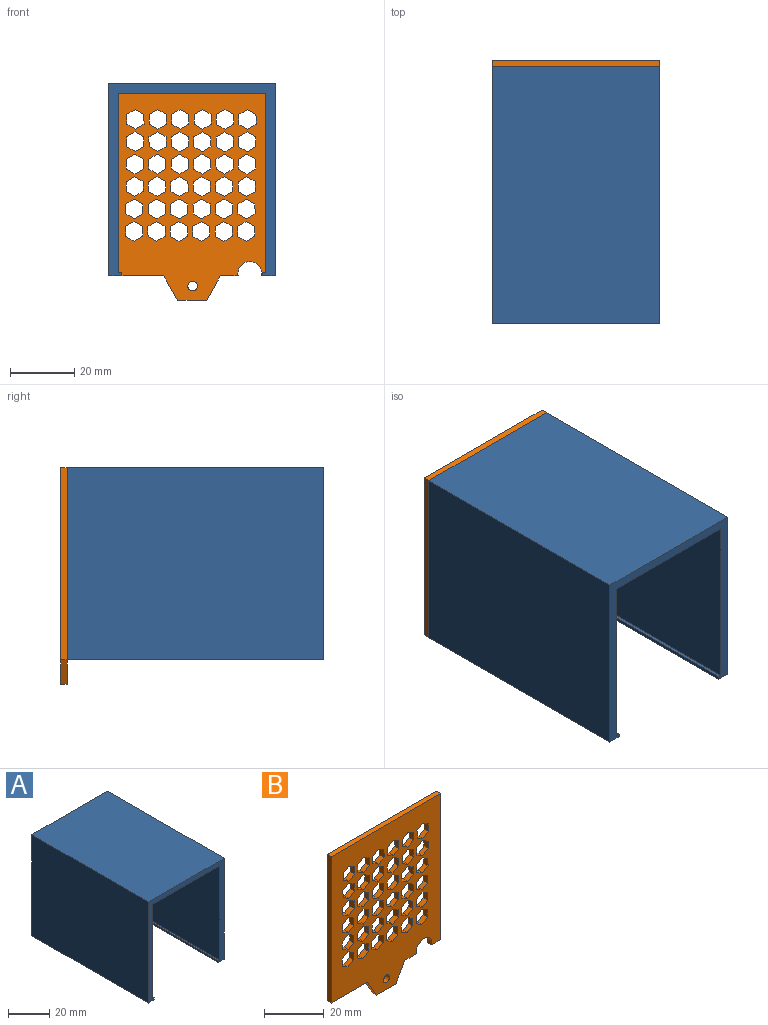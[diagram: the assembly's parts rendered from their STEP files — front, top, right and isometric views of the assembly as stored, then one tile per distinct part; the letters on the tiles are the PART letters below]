
ASSEMBLY  parts=2 mates=1
PART A: 14 faces, bbox 52x80x60 mm
  f0: plane 80x1mm, normal (1,0,0), area 80mm2, adj f1,f11,f12,f13
  f1: plane 80x1mm, normal (0,0,1), area 80mm2, adj f0,f2,f12,f13
  f2: plane 80x56mm, normal (1,0,0), area 4480mm2, adj f1,f3,f12,f13
  f3: plane 80x46mm, normal (0,0,-1), area 3680mm2, adj f2,f4,f12,f13
  f4: plane 80x56mm, normal (-1,0,0), area 4480mm2, adj f3,f5,f12,f13
  f5: plane 80x1mm, normal (0,0,1), area 80mm2, adj f4,f6,f12,f13
  f6: plane 80x1mm, normal (-1,0,0), area 80mm2, adj f5,f7,f12,f13
  f7: plane 80x4mm, normal (0,0,-1), area 320mm2, adj f6,f8,f12,f13
  f8: plane 80x60mm, normal (1,0,0), area 4800mm2, adj f7,f9,f12,f13
  f9: plane 80x52mm, normal (0,0,1), area 4160mm2, adj f8,f10,f12,f13
  f10: plane 80x60mm, normal (-1,0,0), area 4800mm2, adj f9,f11,f12,f13
  f11: plane 80x4mm, normal (0,0,-1), area 320mm2, adj f0,f10,f12,f13
  f12: plane 60x52mm, normal (0,-1,0), area 500mm2, adj f0,f1,f2,f3,f4,f5,f6,f7
  f13: plane 60x52mm, normal (0,1,0), area 500mm2, adj f0,f1,f2,f3,f4,f5,f6,f7
PART B: 229 faces, bbox 52x2x67.5 mm
  f0: plane 5.6x2mm, normal (0,0,-1), area 11.2mm2, adj f3,f4,f224,f228
  f1: plane 4.35x2mm, normal (0,0,-1), area 8.7mm2, adj f3,f4,f5,f228
  f2: plane 17.18x2mm, normal (0,0,-1), area 34.4mm2, adj f3,f4,f7,f225
  f3: plane 67.54x52mm, normal (0,1,0), area 2293.7mm2, adj f0,f1,f2,f5,f6,f7,f8,f9
  f4: plane 67.54x52mm, normal (0,-1,0), area 2293.7mm2, adj f0,f1,f2,f5,f6,f7,f8,f9
  f5: plane 60x2mm, normal (1,0,0), area 120mm2, adj f1,f3,f4,f6
  f6: plane 52x2mm, normal (0,0,1), area 104mm2, adj f3,f4,f5,f7
  f7: plane 60x2mm, normal (-1,0,0), area 120mm2, adj f2,f3,f4,f6
  f8: plane 3.09x2mm, normal (1,0,0.01), area 6.2mm2, adj f3,f4,f9,f13
  f9: plane 2.66x2mm, normal (0.51,0,-0.86), area 6.2mm2, adj f3,f4,f8,f10
  f10: plane 2.69x2mm, normal (-0.49,0,-0.87), area 6.2mm2, adj f3,f4,f9,f11
  f11: plane 3.09x2mm, normal (-1,0,-0.01), area 6.2mm2, adj f3,f4,f10,f12
  f12: plane 2.66x2mm, normal (-0.51,0,0.86), area 6.2mm2, adj f3,f4,f11,f13
  f13: plane 2.69x2mm, normal (0.49,0,0.87), area 6.2mm2, adj f3,f4,f8,f12
  f14: plane 2.66x2mm, normal (0.51,0,-0.86), area 6.2mm2, adj f3,f4,f15,f19
  f15: plane 2.69x2mm, normal (-0.49,0,-0.87), area 6.2mm2, adj f3,f4,f14,f16
  f16: plane 3.09x2mm, normal (-1,0,-0.01), area 6.2mm2, adj f3,f4,f15,f17
  f17: plane 2.66x2mm, normal (-0.51,0,0.86), area 6.2mm2, adj f3,f4,f16,f18
  f18: plane 2.69x2mm, normal (0.49,0,0.87), area 6.2mm2, adj f3,f4,f17,f19
  f19: plane 3.09x2mm, normal (1,0,0.01), area 6.2mm2, adj f3,f4,f14,f18
  f20: plane 3.09x2mm, normal (1,0,0.01), area 6.2mm2, adj f3,f4,f21,f25
  f21: plane 2.66x2mm, normal (0.51,0,-0.86), area 6.2mm2, adj f3,f4,f20,f22
  f22: plane 2.69x2mm, normal (-0.49,0,-0.87), area 6.2mm2, adj f3,f4,f21,f23
  f23: plane 3.09x2mm, normal (-1,0,-0.01), area 6.2mm2, adj f3,f4,f22,f24
  f24: plane 2.66x2mm, normal (-0.51,0,0.86), area 6.2mm2, adj f3,f4,f23,f25
  f25: plane 2.69x2mm, normal (0.49,0,0.87), area 6.2mm2, adj f3,f4,f20,f24
  f26: plane 2.69x2mm, normal (-0.49,0,-0.87), area 6.2mm2, adj f3,f4,f27,f31
  f27: plane 3.09x2mm, normal (-1,0,-0.01), area 6.2mm2, adj f3,f4,f26,f28
  f28: plane 2.66x2mm, normal (-0.51,0,0.86), area 6.2mm2, adj f3,f4,f27,f29
  f29: plane 2.69x2mm, normal (0.49,0,0.87), area 6.2mm2, adj f3,f4,f28,f30
  f30: plane 3.09x2mm, normal (1,0,0.01), area 6.2mm2, adj f3,f4,f29,f31
  f31: plane 2.66x2mm, normal (0.51,0,-0.86), area 6.2mm2, adj f3,f4,f26,f30
  f32: plane 3.09x2mm, normal (-1,0,-0.01), area 6.2mm2, adj f3,f4,f33,f37
  f33: plane 2.66x2mm, normal (-0.51,0,0.86), area 6.2mm2, adj f3,f4,f32,f34
  f34: plane 2.69x2mm, normal (0.49,0,0.87), area 6.2mm2, adj f3,f4,f33,f35
  f35: plane 3.09x2mm, normal (1,0,0.01), area 6.2mm2, adj f3,f4,f34,f36
  f36: plane 2.66x2mm, normal (0.51,0,-0.86), area 6.2mm2, adj f3,f4,f35,f37
  f37: plane 2.69x2mm, normal (-0.49,0,-0.87), area 6.2mm2, adj f3,f4,f32,f36
  f38: plane 2.66x2mm, normal (0.51,0,-0.86), area 6.2mm2, adj f3,f4,f39,f43
  f39: plane 2.69x2mm, normal (-0.49,0,-0.87), area 6.2mm2, adj f3,f4,f38,f40
  f40: plane 3.09x2mm, normal (-1,0,-0.01), area 6.2mm2, adj f3,f4,f39,f41
  f41: plane 2.66x2mm, normal (-0.51,0,0.86), area 6.2mm2, adj f3,f4,f40,f42
  f42: plane 2.69x2mm, normal (0.49,0,0.87), area 6.2mm2, adj f3,f4,f41,f43
  f43: plane 3.09x2mm, normal (1,0,0.01), area 6.2mm2, adj f3,f4,f38,f42
  f44: plane 3.09x2mm, normal (1,0,0.01), area 6.2mm2, adj f3,f4,f45,f49
  f45: plane 2.66x2mm, normal (0.51,0,-0.86), area 6.2mm2, adj f3,f4,f44,f46
  f46: plane 2.69x2mm, normal (-0.49,0,-0.87), area 6.2mm2, adj f3,f4,f45,f47
  f47: plane 3.09x2mm, normal (-1,0,-0.01), area 6.2mm2, adj f3,f4,f46,f48
  f48: plane 2.66x2mm, normal (-0.51,0,0.86), area 6.2mm2, adj f3,f4,f47,f49
  f49: plane 2.69x2mm, normal (0.49,0,0.87), area 6.2mm2, adj f3,f4,f44,f48
  f50: plane 2.69x2mm, normal (-0.49,0,-0.87), area 6.2mm2, adj f3,f4,f51,f55
  f51: plane 3.09x2mm, normal (-1,0,-0.01), area 6.2mm2, adj f3,f4,f50,f52
  f52: plane 2.66x2mm, normal (-0.51,0,0.86), area 6.2mm2, adj f3,f4,f51,f53
  f53: plane 2.69x2mm, normal (0.49,0,0.87), area 6.2mm2, adj f3,f4,f52,f54
  f54: plane 3.09x2mm, normal (1,0,0.01), area 6.2mm2, adj f3,f4,f53,f55
  f55: plane 2.66x2mm, normal (0.51,0,-0.86), area 6.2mm2, adj f3,f4,f50,f54
  f56: plane 2.69x2mm, normal (-0.49,0,-0.87), area 6.2mm2, adj f3,f4,f57,f61
  f57: plane 3.09x2mm, normal (-1,0,-0.01), area 6.2mm2, adj f3,f4,f56,f58
  f58: plane 2.66x2mm, normal (-0.51,0,0.86), area 6.2mm2, adj f3,f4,f57,f59
  f59: plane 2.69x2mm, normal (0.49,0,0.87), area 6.2mm2, adj f3,f4,f58,f60
  f60: plane 3.09x2mm, normal (1,0,0.01), area 6.2mm2, adj f3,f4,f59,f61
  f61: plane 2.66x2mm, normal (0.51,0,-0.86), area 6.2mm2, adj f3,f4,f56,f60
  f62: plane 2.69x2mm, normal (-0.49,0,-0.87), area 6.2mm2, adj f3,f4,f63,f67
  f63: plane 3.09x2mm, normal (-1,0,-0.01), area 6.2mm2, adj f3,f4,f62,f64
  f64: plane 2.66x2mm, normal (-0.51,0,0.86), area 6.2mm2, adj f3,f4,f63,f65
  f65: plane 2.69x2mm, normal (0.49,0,0.87), area 6.2mm2, adj f3,f4,f64,f66
  f66: plane 3.09x2mm, normal (1,0,0.01), area 6.2mm2, adj f3,f4,f65,f67
  f67: plane 2.66x2mm, normal (0.51,0,-0.86), area 6.2mm2, adj f3,f4,f62,f66
  f68: plane 2.69x2mm, normal (-0.49,0,-0.87), area 6.2mm2, adj f3,f4,f69,f73
  f69: plane 3.09x2mm, normal (-1,0,-0.01), area 6.2mm2, adj f3,f4,f68,f70
  f70: plane 2.66x2mm, normal (-0.51,0,0.86), area 6.2mm2, adj f3,f4,f69,f71
  f71: plane 2.69x2mm, normal (0.49,0,0.87), area 6.2mm2, adj f3,f4,f70,f72
  f72: plane 3.09x2mm, normal (1,0,0.01), area 6.2mm2, adj f3,f4,f71,f73
  f73: plane 2.66x2mm, normal (0.51,0,-0.86), area 6.2mm2, adj f3,f4,f68,f72
  f74: plane 3.09x2mm, normal (1,0,0.01), area 6.2mm2, adj f3,f4,f75,f79
  f75: plane 2.66x2mm, normal (0.51,0,-0.86), area 6.2mm2, adj f3,f4,f74,f76
  f76: plane 2.69x2mm, normal (-0.49,0,-0.87), area 6.2mm2, adj f3,f4,f75,f77
  f77: plane 3.09x2mm, normal (-1,0,-0.01), area 6.2mm2, adj f3,f4,f76,f78
  f78: plane 2.66x2mm, normal (-0.51,0,0.86), area 6.2mm2, adj f3,f4,f77,f79
  f79: plane 2.69x2mm, normal (0.49,0,0.87), area 6.2mm2, adj f3,f4,f74,f78
  f80: plane 2.66x2mm, normal (0.51,0,-0.86), area 6.2mm2, adj f3,f4,f81,f85
  f81: plane 2.69x2mm, normal (-0.49,0,-0.87), area 6.2mm2, adj f3,f4,f80,f82
  f82: plane 3.09x2mm, normal (-1,0,-0.01), area 6.2mm2, adj f3,f4,f81,f83
  f83: plane 2.66x2mm, normal (-0.51,0,0.86), area 6.2mm2, adj f3,f4,f82,f84
  f84: plane 2.69x2mm, normal (0.49,0,0.87), area 6.2mm2, adj f3,f4,f83,f85
  f85: plane 3.09x2mm, normal (1,0,0.01), area 6.2mm2, adj f3,f4,f80,f84
  f86: plane 2.66x2mm, normal (0.51,0,-0.86), area 6.2mm2, adj f3,f4,f87,f91
  f87: plane 2.69x2mm, normal (-0.49,0,-0.87), area 6.2mm2, adj f3,f4,f86,f88
  f88: plane 3.09x2mm, normal (-1,0,-0.01), area 6.2mm2, adj f3,f4,f87,f89
  f89: plane 2.66x2mm, normal (-0.51,0,0.86), area 6.2mm2, adj f3,f4,f88,f90
  f90: plane 2.69x2mm, normal (0.49,0,0.87), area 6.2mm2, adj f3,f4,f89,f91
  f91: plane 3.09x2mm, normal (1,0,0.01), area 6.2mm2, adj f3,f4,f86,f90
  f92: plane 2.66x2mm, normal (0.51,0,-0.86), area 6.2mm2, adj f3,f4,f93,f97
  f93: plane 2.69x2mm, normal (-0.49,0,-0.87), area 6.2mm2, adj f3,f4,f92,f94
  f94: plane 3.09x2mm, normal (-1,0,-0.01), area 6.2mm2, adj f3,f4,f93,f95
  f95: plane 2.66x2mm, normal (-0.51,0,0.86), area 6.2mm2, adj f3,f4,f94,f96
  f96: plane 2.69x2mm, normal (0.49,0,0.87), area 6.2mm2, adj f3,f4,f95,f97
  f97: plane 3.09x2mm, normal (1,0,0.01), area 6.2mm2, adj f3,f4,f92,f96
  f98: plane 2.66x2mm, normal (0.51,0,-0.86), area 6.2mm2, adj f3,f4,f99,f103
  f99: plane 2.69x2mm, normal (-0.49,0,-0.87), area 6.2mm2, adj f3,f4,f98,f100
  f100: plane 3.09x2mm, normal (-1,0,-0.01), area 6.2mm2, adj f3,f4,f99,f101
  f101: plane 2.66x2mm, normal (-0.51,0,0.86), area 6.2mm2, adj f3,f4,f100,f102
  f102: plane 2.69x2mm, normal (0.49,0,0.87), area 6.2mm2, adj f3,f4,f101,f103
  f103: plane 3.09x2mm, normal (1,0,0.01), area 6.2mm2, adj f3,f4,f98,f102
  f104: plane 2.66x2mm, normal (0.51,0,-0.86), area 6.2mm2, adj f3,f4,f105,f109
  f105: plane 2.69x2mm, normal (-0.49,0,-0.87), area 6.2mm2, adj f3,f4,f104,f106
  f106: plane 3.09x2mm, normal (-1,0,-0.01), area 6.2mm2, adj f3,f4,f105,f107
  f107: plane 2.66x2mm, normal (-0.51,0,0.86), area 6.2mm2, adj f3,f4,f106,f108
  f108: plane 2.69x2mm, normal (0.49,0,0.87), area 6.2mm2, adj f3,f4,f107,f109
  f109: plane 3.09x2mm, normal (1,0,0.01), area 6.2mm2, adj f3,f4,f104,f108
  f110: plane 3.09x2mm, normal (-1,0,-0.01), area 6.2mm2, adj f3,f4,f111,f115
  f111: plane 2.66x2mm, normal (-0.51,0,0.86), area 6.2mm2, adj f3,f4,f110,f112
  f112: plane 2.69x2mm, normal (0.49,0,0.87), area 6.2mm2, adj f3,f4,f111,f113
  f113: plane 3.09x2mm, normal (1,0,0.01), area 6.2mm2, adj f3,f4,f112,f114
  f114: plane 2.66x2mm, normal (0.51,0,-0.86), area 6.2mm2, adj f3,f4,f113,f115
  f115: plane 2.69x2mm, normal (-0.49,0,-0.87), area 6.2mm2, adj f3,f4,f110,f114
  f116: plane 2.69x2mm, normal (-0.49,0,-0.87), area 6.2mm2, adj f3,f4,f117,f121
  f117: plane 3.09x2mm, normal (-1,0,-0.01), area 6.2mm2, adj f3,f4,f116,f118
  f118: plane 2.66x2mm, normal (-0.51,0,0.86), area 6.2mm2, adj f3,f4,f117,f119
  f119: plane 2.69x2mm, normal (0.49,0,0.87), area 6.2mm2, adj f3,f4,f118,f120
  f120: plane 3.09x2mm, normal (1,0,0.01), area 6.2mm2, adj f3,f4,f119,f121
  f121: plane 2.66x2mm, normal (0.51,0,-0.86), area 6.2mm2, adj f3,f4,f116,f120
  f122: plane 2.69x2mm, normal (-0.49,0,-0.87), area 6.2mm2, adj f3,f4,f123,f127
  f123: plane 3.09x2mm, normal (-1,0,-0.01), area 6.2mm2, adj f3,f4,f122,f124
  f124: plane 2.66x2mm, normal (-0.51,0,0.86), area 6.2mm2, adj f3,f4,f123,f125
  f125: plane 2.69x2mm, normal (0.49,0,0.87), area 6.2mm2, adj f3,f4,f124,f126
  f126: plane 3.09x2mm, normal (1,0,0.01), area 6.2mm2, adj f3,f4,f125,f127
  f127: plane 2.66x2mm, normal (0.51,0,-0.86), area 6.2mm2, adj f3,f4,f122,f126
  f128: plane 2.69x2mm, normal (-0.49,0,-0.87), area 6.2mm2, adj f3,f4,f129,f133
  f129: plane 3.09x2mm, normal (-1,0,-0.01), area 6.2mm2, adj f3,f4,f128,f130
  f130: plane 2.66x2mm, normal (-0.51,0,0.86), area 6.2mm2, adj f3,f4,f129,f131
  f131: plane 2.69x2mm, normal (0.49,0,0.87), area 6.2mm2, adj f3,f4,f130,f132
  f132: plane 3.09x2mm, normal (1,0,0.01), area 6.2mm2, adj f3,f4,f131,f133
  f133: plane 2.66x2mm, normal (0.51,0,-0.86), area 6.2mm2, adj f3,f4,f128,f132
  f134: plane 2.69x2mm, normal (-0.49,0,-0.87), area 6.2mm2, adj f3,f4,f135,f139
  f135: plane 3.09x2mm, normal (-1,0,-0.01), area 6.2mm2, adj f3,f4,f134,f136
  f136: plane 2.66x2mm, normal (-0.51,0,0.86), area 6.2mm2, adj f3,f4,f135,f137
  f137: plane 2.69x2mm, normal (0.49,0,0.87), area 6.2mm2, adj f3,f4,f136,f138
  f138: plane 3.09x2mm, normal (1,0,0.01), area 6.2mm2, adj f3,f4,f137,f139
  f139: plane 2.66x2mm, normal (0.51,0,-0.86), area 6.2mm2, adj f3,f4,f134,f138
  f140: plane 2.69x2mm, normal (-0.49,0,-0.87), area 6.2mm2, adj f3,f4,f141,f145
  f141: plane 3.09x2mm, normal (-1,0,-0.01), area 6.2mm2, adj f3,f4,f140,f142
  f142: plane 2.66x2mm, normal (-0.51,0,0.86), area 6.2mm2, adj f3,f4,f141,f143
  f143: plane 2.69x2mm, normal (0.49,0,0.87), area 6.2mm2, adj f3,f4,f142,f144
  f144: plane 3.09x2mm, normal (1,0,0.01), area 6.2mm2, adj f3,f4,f143,f145
  f145: plane 2.66x2mm, normal (0.51,0,-0.86), area 6.2mm2, adj f3,f4,f140,f144
  f146: plane 3.09x2mm, normal (1,0,0.01), area 6.2mm2, adj f3,f4,f147,f151
  f147: plane 2.66x2mm, normal (0.51,0,-0.86), area 6.2mm2, adj f3,f4,f146,f148
  f148: plane 2.69x2mm, normal (-0.49,0,-0.87), area 6.2mm2, adj f3,f4,f147,f149
  f149: plane 3.09x2mm, normal (-1,0,-0.01), area 6.2mm2, adj f3,f4,f148,f150
  f150: plane 2.66x2mm, normal (-0.51,0,0.86), area 6.2mm2, adj f3,f4,f149,f151
  f151: plane 2.69x2mm, normal (0.49,0,0.87), area 6.2mm2, adj f3,f4,f146,f150
  f152: plane 2.69x2mm, normal (-0.49,0,-0.87), area 6.2mm2, adj f3,f4,f153,f157
  f153: plane 3.09x2mm, normal (-1,0,-0.01), area 6.2mm2, adj f3,f4,f152,f154
  f154: plane 2.66x2mm, normal (-0.51,0,0.86), area 6.2mm2, adj f3,f4,f153,f155
  f155: plane 2.69x2mm, normal (0.49,0,0.87), area 6.2mm2, adj f3,f4,f154,f156
  f156: plane 3.09x2mm, normal (1,0,0.01), area 6.2mm2, adj f3,f4,f155,f157
  f157: plane 2.66x2mm, normal (0.51,0,-0.86), area 6.2mm2, adj f3,f4,f152,f156
  f158: plane 2.69x2mm, normal (-0.49,0,-0.87), area 6.2mm2, adj f3,f4,f159,f163
  f159: plane 3.09x2mm, normal (-1,0,-0.01), area 6.2mm2, adj f3,f4,f158,f160
  f160: plane 2.66x2mm, normal (-0.51,0,0.86), area 6.2mm2, adj f3,f4,f159,f161
  f161: plane 2.69x2mm, normal (0.49,0,0.87), area 6.2mm2, adj f3,f4,f160,f162
  f162: plane 3.09x2mm, normal (1,0,0.01), area 6.2mm2, adj f3,f4,f161,f163
  f163: plane 2.66x2mm, normal (0.51,0,-0.86), area 6.2mm2, adj f3,f4,f158,f162
  f164: plane 3.09x2mm, normal (-1,0,-0.01), area 6.2mm2, adj f3,f4,f165,f169
  f165: plane 2.66x2mm, normal (-0.51,0,0.86), area 6.2mm2, adj f3,f4,f164,f166
  f166: plane 2.69x2mm, normal (0.49,0,0.87), area 6.2mm2, adj f3,f4,f165,f167
  f167: plane 3.09x2mm, normal (1,0,0.01), area 6.2mm2, adj f3,f4,f166,f168
  f168: plane 2.66x2mm, normal (0.51,0,-0.86), area 6.2mm2, adj f3,f4,f167,f169
  f169: plane 2.69x2mm, normal (-0.49,0,-0.87), area 6.2mm2, adj f3,f4,f164,f168
  f170: plane 2.66x2mm, normal (0.51,0,-0.86), area 6.2mm2, adj f3,f4,f171,f175
  f171: plane 2.69x2mm, normal (-0.49,0,-0.87), area 6.2mm2, adj f3,f4,f170,f172
  f172: plane 3.09x2mm, normal (-1,0,-0.01), area 6.2mm2, adj f3,f4,f171,f173
  f173: plane 2.66x2mm, normal (-0.51,0,0.86), area 6.2mm2, adj f3,f4,f172,f174
  f174: plane 2.69x2mm, normal (0.49,0,0.87), area 6.2mm2, adj f3,f4,f173,f175
  f175: plane 3.09x2mm, normal (1,0,0.01), area 6.2mm2, adj f3,f4,f170,f174
  f176: plane 2.69x2mm, normal (-0.49,0,-0.87), area 6.2mm2, adj f3,f4,f177,f181
  f177: plane 3.09x2mm, normal (-1,0,-0.01), area 6.2mm2, adj f3,f4,f176,f178
  f178: plane 2.66x2mm, normal (-0.51,0,0.86), area 6.2mm2, adj f3,f4,f177,f179
  f179: plane 2.69x2mm, normal (0.49,0,0.87), area 6.2mm2, adj f3,f4,f178,f180
  f180: plane 3.09x2mm, normal (1,0,0.01), area 6.2mm2, adj f3,f4,f179,f181
  f181: plane 2.66x2mm, normal (0.51,0,-0.86), area 6.2mm2, adj f3,f4,f176,f180
  f182: plane 2.69x2mm, normal (-0.49,0,-0.87), area 6.2mm2, adj f3,f4,f183,f187
  f183: plane 3.09x2mm, normal (-1,0,-0.01), area 6.2mm2, adj f3,f4,f182,f184
  f184: plane 2.66x2mm, normal (-0.51,0,0.86), area 6.2mm2, adj f3,f4,f183,f185
  f185: plane 2.69x2mm, normal (0.49,0,0.87), area 6.2mm2, adj f3,f4,f184,f186
  f186: plane 3.09x2mm, normal (1,0,0.01), area 6.2mm2, adj f3,f4,f185,f187
  f187: plane 2.66x2mm, normal (0.51,0,-0.86), area 6.2mm2, adj f3,f4,f182,f186
  f188: plane 3.09x2mm, normal (-1,0,-0.01), area 6.2mm2, adj f3,f4,f189,f193
  f189: plane 2.66x2mm, normal (-0.51,0,0.86), area 6.2mm2, adj f3,f4,f188,f190
  f190: plane 2.69x2mm, normal (0.49,0,0.87), area 6.2mm2, adj f3,f4,f189,f191
  f191: plane 3.09x2mm, normal (1,0,0.01), area 6.2mm2, adj f3,f4,f190,f192
  f192: plane 2.66x2mm, normal (0.51,0,-0.86), area 6.2mm2, adj f3,f4,f191,f193
  f193: plane 2.69x2mm, normal (-0.49,0,-0.87), area 6.2mm2, adj f3,f4,f188,f192
  f194: plane 2.66x2mm, normal (0.51,0,-0.86), area 6.2mm2, adj f3,f4,f195,f199
  f195: plane 2.69x2mm, normal (-0.49,0,-0.87), area 6.2mm2, adj f3,f4,f194,f196
  f196: plane 3.09x2mm, normal (-1,0,-0.01), area 6.2mm2, adj f3,f4,f195,f197
  f197: plane 2.66x2mm, normal (-0.51,0,0.86), area 6.2mm2, adj f3,f4,f196,f198
  f198: plane 2.69x2mm, normal (0.49,0,0.87), area 6.2mm2, adj f3,f4,f197,f199
  f199: plane 3.09x2mm, normal (1,0,0.01), area 6.2mm2, adj f3,f4,f194,f198
  f200: plane 3.09x2mm, normal (-1,0,-0.01), area 6.2mm2, adj f3,f4,f201,f205
  f201: plane 2.66x2mm, normal (-0.51,0,0.86), area 6.2mm2, adj f3,f4,f200,f202
  f202: plane 2.69x2mm, normal (0.49,0,0.87), area 6.2mm2, adj f3,f4,f201,f203
  f203: plane 3.09x2mm, normal (1,0,0.01), area 6.2mm2, adj f3,f4,f202,f204
  f204: plane 2.66x2mm, normal (0.51,0,-0.86), area 6.2mm2, adj f3,f4,f203,f205
  f205: plane 2.69x2mm, normal (-0.49,0,-0.87), area 6.2mm2, adj f3,f4,f200,f204
  f206: plane 2.66x2mm, normal (0.51,0,-0.86), area 6.2mm2, adj f3,f4,f207,f211
  f207: plane 2.69x2mm, normal (-0.49,0,-0.87), area 6.2mm2, adj f3,f4,f206,f208
  f208: plane 3.09x2mm, normal (-1,0,-0.01), area 6.2mm2, adj f3,f4,f207,f209
  f209: plane 2.66x2mm, normal (-0.51,0,0.86), area 6.2mm2, adj f3,f4,f208,f210
  f210: plane 2.69x2mm, normal (0.49,0,0.87), area 6.2mm2, adj f3,f4,f209,f211
  f211: plane 3.09x2mm, normal (1,0,0.01), area 6.2mm2, adj f3,f4,f206,f210
  f212: plane 3.09x2mm, normal (1,0,0.01), area 6.2mm2, adj f3,f4,f213,f217
  f213: plane 2.66x2mm, normal (0.51,0,-0.86), area 6.2mm2, adj f3,f4,f212,f214
  f214: plane 2.69x2mm, normal (-0.49,0,-0.87), area 6.2mm2, adj f3,f4,f213,f215
  f215: plane 3.09x2mm, normal (-1,0,-0.01), area 6.2mm2, adj f3,f4,f214,f216
  f216: plane 2.66x2mm, normal (-0.51,0,0.86), area 6.2mm2, adj f3,f4,f215,f217
  f217: plane 2.69x2mm, normal (0.49,0,0.87), area 6.2mm2, adj f3,f4,f212,f216
  f218: plane 2.69x2mm, normal (-0.49,0,-0.87), area 6.2mm2, adj f3,f4,f219,f223
  f219: plane 3.09x2mm, normal (-1,0,-0.01), area 6.2mm2, adj f3,f4,f218,f220
  f220: plane 2.66x2mm, normal (-0.51,0,0.86), area 6.2mm2, adj f3,f4,f219,f221
  f221: plane 2.69x2mm, normal (0.49,0,0.87), area 6.2mm2, adj f3,f4,f220,f222
  f222: plane 3.09x2mm, normal (1,0,0.01), area 6.2mm2, adj f3,f4,f221,f223
  f223: plane 2.66x2mm, normal (0.51,0,-0.86), area 6.2mm2, adj f3,f4,f218,f222
  f224: plane 7.54x4.25mm, normal (0.87,0,-0.49), area 17.3mm2, adj f0,f3,f4,f227
  f225: plane 7.54x4.36mm, normal (-0.87,0,-0.5), area 17.4mm2, adj f2,f3,f4,f227
  f226: cylinder r=1.5mm len=3mm, axis (0,-1,0), area 18.8mm2, adj f3,f4
  f227: plane 9.06x2mm, normal (0,0,-1), area 18.1mm2, adj f3,f4,f224,f225
  f228: cylinder r=3.7mm len=7.4mm, axis (0,1,0), area 26.5mm2, adj f0,f1,f3,f4
PLACE A t=(-57.17,14.97,-22.7)mm
PLACE B t=(-119.72,14.97,-108.67)mm
MATE fastened A.f13 <-> B.f4  axis (0,-1,0) through (-34.38,14.97,-13.76)mm
